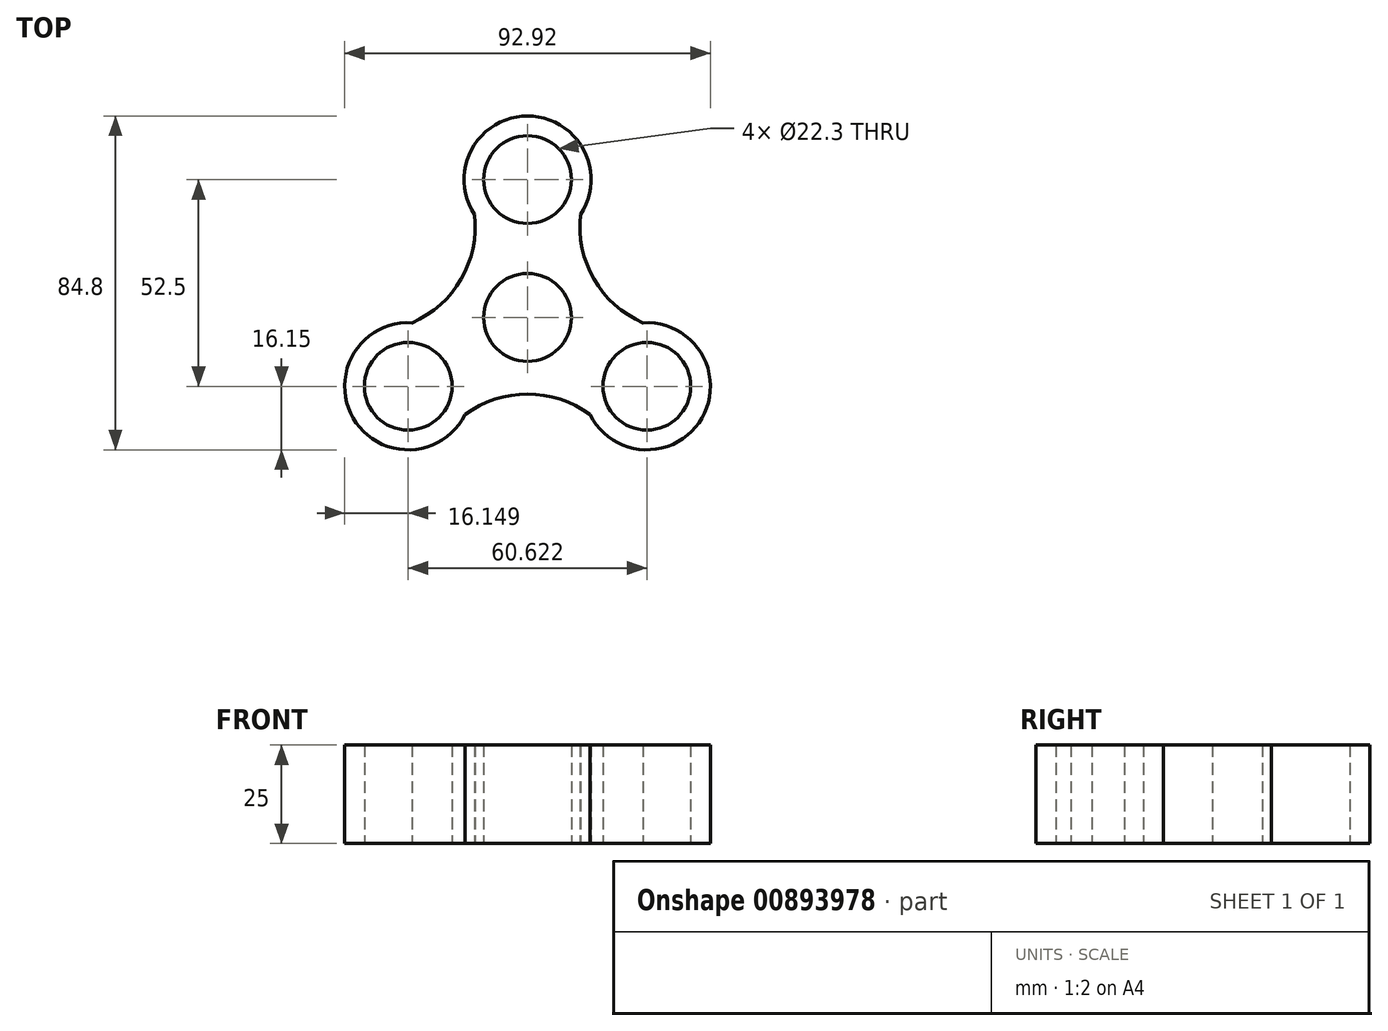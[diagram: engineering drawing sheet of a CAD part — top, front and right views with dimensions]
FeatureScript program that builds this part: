
annotation { "Feature Type Name" : "Feature", "Feature Type Description" : "" }
export const myFeature = defineFeature(function(context is Context, id is Id, definition is map)
    precondition{}
    {
        {
            var Q0;
            Q0=qCreatedBy(makeId("Top.planeOp"),FACE);
            var sketch = newSketch(context, id + "F0", { "sketchPlane" : qUnion([Q0])});
            skCircle(sketch, "E0", {"center": v(0, 0) * mm, "radius": 11.15 * mm});
            skLineSegment(sketch, "E1", {"start": v(0, 0) * mm, "end": v(0, 11.15) * mm});
            skCircle(sketch, "E2", {"center": v(0, 35) * mm, "radius": 11.15 * mm});
            skCircle(sketch, "E3.1.0", {"center": v(-30.31, -17.5) * mm, "radius": 11.15 * mm});
            skCircle(sketch, "E3.2.0", {"center": v(30.31, -17.5) * mm, "radius": 11.15 * mm});
            skArc(sketch, "E4.0", {"start": v(13.48, 26.11) * mm, "mid": v(0, 51.15) * mm, "end": v(-13.48, 26.11) * mm});
            skArc(sketch, "E5.0", {"start": v(15.87, -24.73) * mm, "mid": v(44.3, -25.58) * mm, "end": v(29.35, -1.38) * mm});
            skArc(sketch, "E6.0", {"start": v(-29.35, -1.38) * mm, "mid": v(-44.3, -25.57) * mm, "end": v(-15.87, -24.73) * mm});
            skLineSegment(sketch, "E7", {"start": v(-11.15, 35) * mm, "end": v(-16.15, 35) * mm, "construction": true});
            skArc(sketch, "E8", {"start": v(-29.35, -1.38) * mm, "mid": v(-16.87, 9.74) * mm, "end": v(-13.48, 26.11) * mm});
            skArc(sketch, "E9.1.0", {"start": v(15.87, -24.73) * mm, "mid": v(0, -19.48) * mm, "end": v(-15.87, -24.73) * mm});
            skArc(sketch, "E9.2.0", {"start": v(13.48, 26.11) * mm, "mid": v(16.87, 9.74) * mm, "end": v(29.35, -1.38) * mm});
            skPoint(sketch, "E10.orphan", {"position": v(-38.39, -3.51) * mm});
            skPoint(sketch, "E11.orphan", {"position": v(-22.24, -31.49) * mm});
            skPoint(sketch, "E12.orphan", {"position": v(22.24, -31.49) * mm});
            skPoint(sketch, "E13.orphan", {"position": v(16.15, 35) * mm});
            skPoint(sketch, "E14.orphan", {"position": v(38.39, -3.51) * mm});
            skLineSegment(sketch, "E15", {"start": v(0, -33.54) * mm, "end": v(0, 51.15) * mm});
            skLineSegment(sketch, "E16", {"start": v(1.88, 0) * mm, "end": v(-30.31, -17.5) * mm});
            skLineSegment(sketch, "E17", {"start": v(1.88, 0) * mm, "end": v(0, 0) * mm});
            skLineSegment(sketch, "E18", {"start": v(30.31, -17.5) * mm, "end": v(0, 0) * mm});
            skLineSegment(sketch, "E19", {"start": v(0, 0) * mm, "end": v(30.31, -17.5) * mm});
            skSolve(sketch);
        }
        {
            var Q0;
            Q0 = qSketchRegion(id + "F0", true);
            extrude(context, id + "F1", {"entities" : qUnion([Q0]), "depth" : 7 * mm, "offsetDistance" : 25 * mm});
        }
        {
            var Q0;
            Q0 = qSketchRegion(id + "F0", true);
            extrude(context, id + "F2", {"entities" : qUnion([Q0]), "operationType" : NewBodyOperationType.ADD, "depth" : 25 * mm, "offsetDistance" : 25 * mm});
        }
    });
